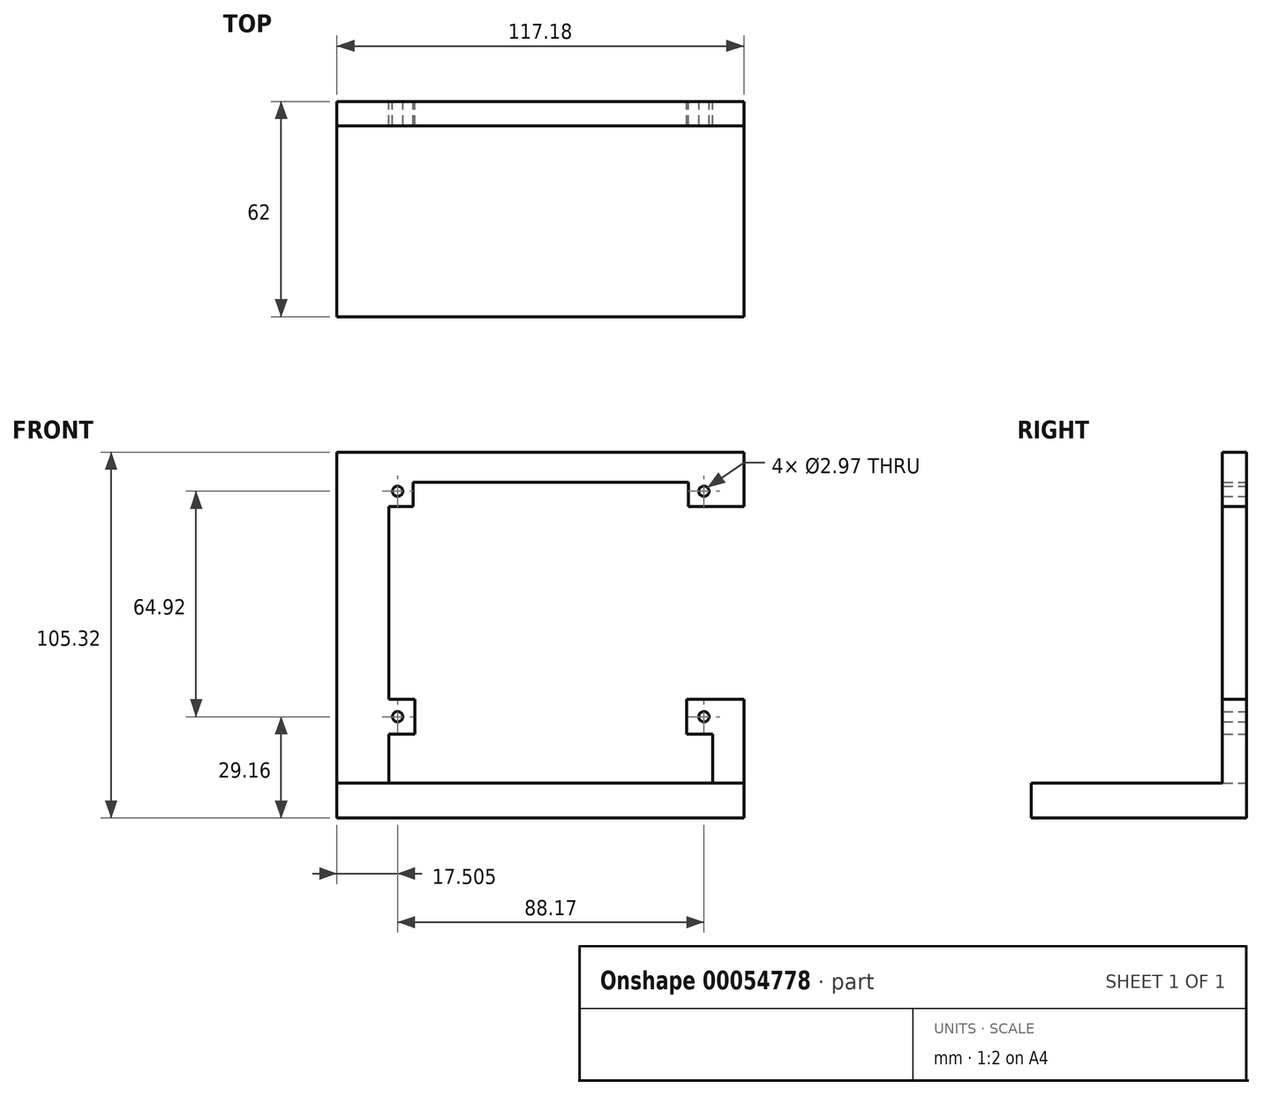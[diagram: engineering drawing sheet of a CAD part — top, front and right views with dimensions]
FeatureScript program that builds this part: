
annotation { "Feature Type Name" : "Feature", "Feature Type Description" : "" }
export const myFeature = defineFeature(function(context is Context, id is Id, definition is map)
    precondition{}
    {
        {
            var Q0;
            Q0=qCreatedBy(makeId("Front.planeOp"),FACE);
            var sketch = newSketch(context, id + "F0", { "sketchPlane" : qUnion([Q0])});
            skCircle(sketch, "E0", {"center": v(-44.09, 0) * mm, "radius": 1.49 * mm});
            skCircle(sketch, "E1", {"center": v(44.09, 0) * mm, "radius": 1.49 * mm});
            skCircle(sketch, "E2", {"center": v(-44.09, 64.92) * mm, "radius": 1.49 * mm});
            skCircle(sketch, "E3", {"center": v(44.08, 64.92) * mm, "radius": 1.49 * mm});
            skLineSegment(sketch, "E4.bottom", {"start": v(-39.6, 67.53) * mm, "end": v(39.6, 67.53) * mm});
            skLineSegment(sketch, "E4.top", {"start": v(-46.59, -19.16) * mm, "end": v(46.59, -19.16) * mm});
            skLineSegment(sketch, "E4.left", {"start": v(-46.6, 60.53) * mm, "end": v(-46.6, 5) * mm});
            skLineSegment(sketch, "E4.right", {"start": v(46.59, 60.54) * mm, "end": v(46.59, 5) * mm});
            skLineSegment(sketch, "E5.top", {"start": v(-46.6, 60.53) * mm, "end": v(-39.6, 60.53) * mm});
            skLineSegment(sketch, "E5.right", {"start": v(-39.6, 67.53) * mm, "end": v(-39.6, 60.53) * mm});
            skLineSegment(sketch, "E6.top", {"start": v(46.59, 60.53) * mm, "end": v(39.6, 60.53) * mm});
            skLineSegment(sketch, "E6.right", {"start": v(39.59, 67.53) * mm, "end": v(39.6, 60.53) * mm});
            skLineSegment(sketch, "E7.bottom", {"start": v(46.59, -5) * mm, "end": v(39.08, -5) * mm});
            skLineSegment(sketch, "E7.top", {"start": v(46.59, 5) * mm, "end": v(39.08, 5) * mm});
            skLineSegment(sketch, "E7.right", {"start": v(39.08, -5) * mm, "end": v(39.08, 5) * mm});
            skLineSegment(sketch, "E8.bottom", {"start": v(-46.6, 5) * mm, "end": v(-39.09, 5) * mm});
            skLineSegment(sketch, "E8.top", {"start": v(-46.6, -5) * mm, "end": v(-39.09, -5) * mm});
            skLineSegment(sketch, "E8.right", {"start": v(-39.09, 5) * mm, "end": v(-39.09, -5) * mm});
            skLineSegment(sketch, "E9", {"start": v(-61.59, -19.16) * mm, "end": v(-61.6, 76.16) * mm});
            skLineSegment(sketch, "E10", {"start": v(-61.6, 76.16) * mm, "end": v(55.59, 76.16) * mm});
            skLineSegment(sketch, "E11", {"start": v(55.59, 76.16) * mm, "end": v(55.59, 60.53) * mm});
            skLineSegment(sketch, "E12", {"start": v(55.59, 60.53) * mm, "end": v(46.59, 60.53) * mm});
            skLineSegment(sketch, "E13", {"start": v(55.59, -19.16) * mm, "end": v(55.59, 5) * mm});
            skLineSegment(sketch, "E14", {"start": v(55.59, 5) * mm, "end": v(46.59, 5) * mm});
            skLineSegment(sketch, "E15", {"start": v(-61.59, -19.16) * mm, "end": v(-61.59, -29.16) * mm});
            skLineSegment(sketch, "E16", {"start": v(-61.59, -29.16) * mm, "end": v(55.6, -29.15) * mm});
            skLineSegment(sketch, "E17", {"start": v(55.6, -19.16) * mm, "end": v(55.6, -29.15) * mm});
            skLineSegment(sketch, "E18.trimOffspring", {"start": v(46.59, -5) * mm, "end": v(46.59, -19.16) * mm});
            skPoint(sketch, "E6.left.start.orphan", {"position": v(46.59, 67.53) * mm});
            skLineSegment(sketch, "E19.trimOffspring", {"start": v(-46.6, -5) * mm, "end": v(-46.6, -19.16) * mm});
            skSolve(sketch);
        }
        {
            var Q0;
            Q0=makeQuery(id+"F0.imprint","IMPRINT",FACE,{"disambiguationData":[TD([[makeQuery(id+"F0.imprint","IMPRINT",EDGE,{"derivedFrom":sQuery(id+"F0.wireOp",EDGE,"E0")}),-1.0]])]});
            extrude(context, id + "F1", {"entities" : qUnion([Q0]), "depth" : 7 * mm});
        }
        {
            var Q0;
            Q0=makeQuery(id+"F1.opExtrude","CAP_FACE",FACE,{"disambiguationData":[OSD([sQuery(id+"F0.wireOp",EDGE,"E0"),sQuery(id+"F0.wireOp",EDGE,"E1"),sQuery(id+"F0.wireOp",EDGE,"E2"),sQuery(id+"F0.wireOp",EDGE,"E3"),sQuery(id+"F0.wireOp",EDGE,"E4.bottom"),sQuery(id+"F0.wireOp",EDGE,"E4.top"),sQuery(id+"F0.wireOp",EDGE,"E4.left"),sQuery(id+"F0.wireOp",EDGE,"E5.top"),sQuery(id+"F0.wireOp",EDGE,"E5.right"),sQuery(id+"F0.wireOp",EDGE,"E6.top"),sQuery(id+"F0.wireOp",EDGE,"E6.right"),sQuery(id+"F0.wireOp",EDGE,"E7.bottom"),sQuery(id+"F0.wireOp",EDGE,"E7.top"),sQuery(id+"F0.wireOp",EDGE,"E7.right"),sQuery(id+"F0.wireOp",EDGE,"E8.bottom"),sQuery(id+"F0.wireOp",EDGE,"E8.top"),sQuery(id+"F0.wireOp",EDGE,"E8.right"),sQuery(id+"F0.wireOp",EDGE,"E9"),sQuery(id+"F0.wireOp",EDGE,"E10"),sQuery(id+"F0.wireOp",EDGE,"E11"),sQuery(id+"F0.wireOp",EDGE,"E12"),sQuery(id+"F0.wireOp",EDGE,"E13"),sQuery(id+"F0.wireOp",EDGE,"E14"),sQuery(id+"F0.wireOp",EDGE,"E15"),sQuery(id+"F0.wireOp",EDGE,"E16"),sQuery(id+"F0.wireOp",EDGE,"E17"),sQuery(id+"F0.wireOp",EDGE,"E18.trimOffspring"),sQuery(id+"F0.wireOp",EDGE,"E19.trimOffspring")])],"isStart":false});
            var sketch = newSketch(context, id + "F2", { "sketchPlane" : qUnion([Q0])});
            skLineSegment(sketch, "E20.bottom", {"start": v(-61.6, -29.16) * mm, "end": v(55.6, -29.16) * mm});
            skLineSegment(sketch, "E20.top", {"start": v(-61.59, -19.15) * mm, "end": v(55.6, -19.15) * mm});
            skLineSegment(sketch, "E20.left", {"start": v(-61.59, -29.16) * mm, "end": v(-61.59, -19.15) * mm});
            skLineSegment(sketch, "E20.right", {"start": v(55.6, -29.16) * mm, "end": v(55.6, -19.15) * mm});
            skSolve(sketch);
        }
        {
            var Q0;
            Q0=makeQuery(id+"F2.imprint","IMPRINT",FACE,{"disambiguationData":[TD([[makeQuery(id+"F2.imprint","IMPRINT",EDGE,{"derivedFrom":sQuery(id+"F2.wireOp",EDGE,"E20.bottom")}),1.0]])]});
            extrude(context, id + "F3", {"entities" : qUnion([Q0]), "operationType" : NewBodyOperationType.ADD, "depth" : 55 * mm});
        }
    });
